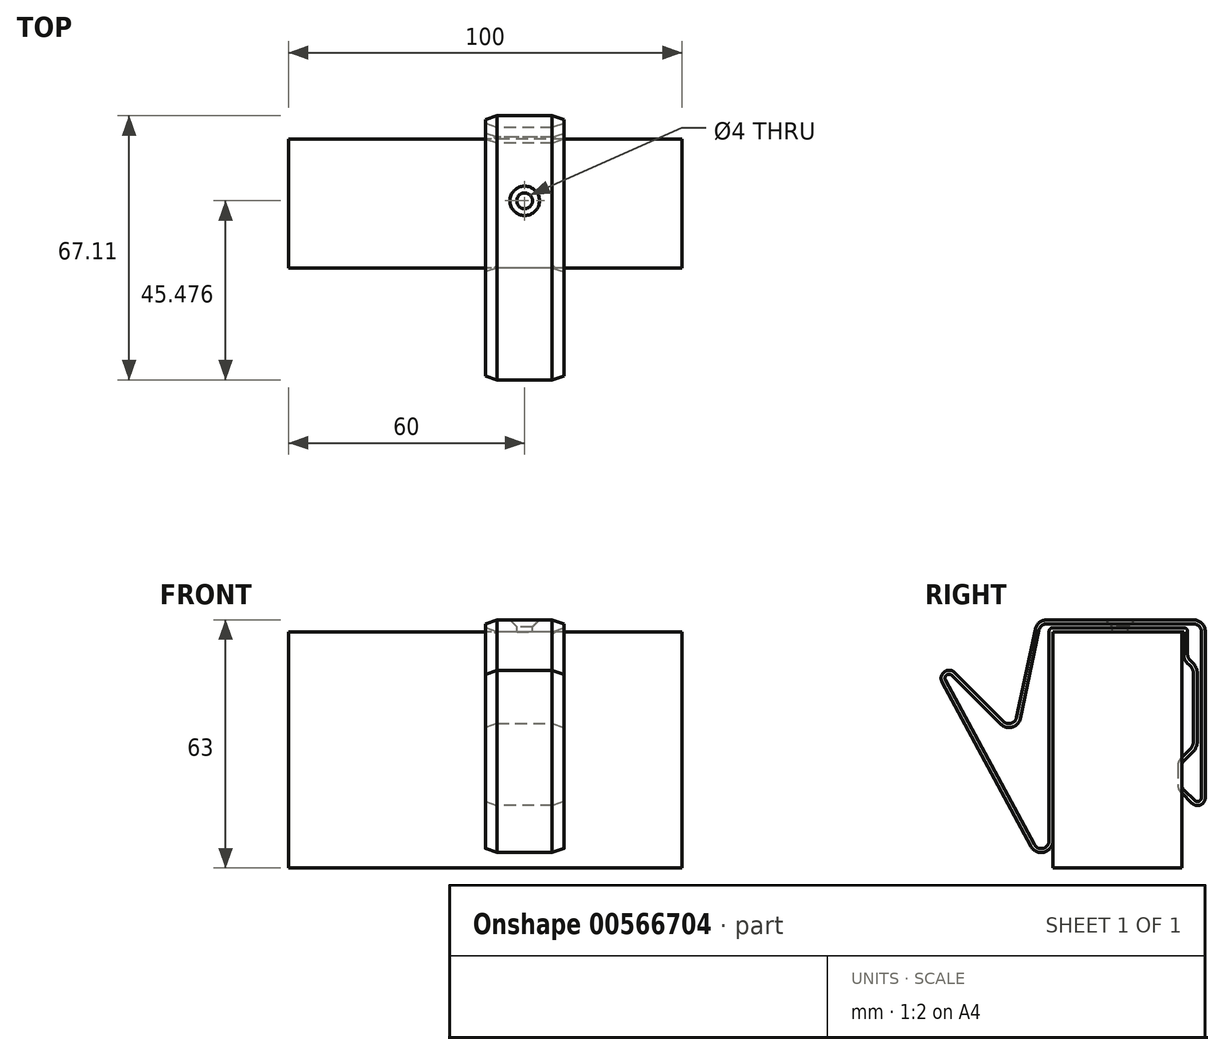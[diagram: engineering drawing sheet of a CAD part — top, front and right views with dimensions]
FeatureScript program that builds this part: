
annotation { "Feature Type Name" : "Feature", "Feature Type Description" : "" }
export const myFeature = defineFeature(function(context is Context, id is Id, definition is map)
    precondition{}
    {
        {
            var Q0;
            Q0=qCreatedBy(makeId("Right.planeOp"),FACE);
            var sketch = newSketch(context, id + "F0", { "sketchPlane" : qUnion([Q0])});
            skLineSegment(sketch, "E0.bottom", {"start": v(0, 0) * mm, "end": v(32.7, 0) * mm});
            skLineSegment(sketch, "E0.top", {"start": v(0, -60) * mm, "end": v(32.7, -60) * mm});
            skLineSegment(sketch, "E0.left", {"start": v(0, 0) * mm, "end": v(0, -60) * mm});
            skLineSegment(sketch, "E0.right", {"start": v(32.7, 0) * mm, "end": v(32.7, -60) * mm});
            skSolve(sketch);
        }
        {
            var Q0;
            Q0=qSketchRegion(id+"F0",true);
            extrude(context, id + "F1", {"entities" : qUnion([Q0]), "depth" : 50 * mm, "hasSecondDirection" : true, "secondDirectionOppositeDirection" : true, "secondDirectionDepth" : 50 * mm});
        }
        {
            var Q0;
            Q0=qCreatedBy(makeId("Right.planeOp"),FACE);
            var sketch = newSketch(context, id + "F2", { "sketchPlane" : qUnion([Q0])});
            skLineSegment(sketch, "E1", {"start": v(0, -65) * mm, "end": v(-28.17, -12.75) * mm});
            skLineSegment(sketch, "E2", {"start": v(-25, -10.38) * mm, "end": v(-10, -25.38) * mm});
            skLineSegment(sketch, "E3", {"start": v(-10, -25.38) * mm, "end": v(-4, 3) * mm});
            skLineSegment(sketch, "E4", {"start": v(-4, 3) * mm, "end": v(38.7, 3) * mm});
            skLineSegment(sketch, "E5", {"start": v(38.7, 3) * mm, "end": v(38.7, -47) * mm});
            skLineSegment(sketch, "E6", {"start": v(38.7, -47) * mm, "end": v(31.7, -40) * mm});
            skLineSegment(sketch, "E7", {"start": v(31.7, -40) * mm, "end": v(31.7, -33) * mm});
            skLineSegment(sketch, "E8", {"start": v(31.7, -33) * mm, "end": v(35.7, -29) * mm});
            skLineSegment(sketch, "E9", {"start": v(35.7, -29) * mm, "end": v(35.7, -9.5) * mm});
            skLineSegment(sketch, "E10", {"start": v(35.7, -9.5) * mm, "end": v(33.2, -7) * mm});
            skLineSegment(sketch, "E11", {"start": v(33.2, -7) * mm, "end": v(33.2, 0) * mm});
            skLineSegment(sketch, "E12", {"start": v(33.2, 0) * mm, "end": v(0, 0) * mm});
            skLineSegment(sketch, "E13", {"start": v(0, 0) * mm, "end": v(0, -65) * mm});
            skArc(sketch, "E14", {"start": v(-25, -10.38) * mm, "mid": v(-27.6, -10.2) * mm, "end": v(-28.17, -12.75) * mm});
            skSolve(sketch);
        }
        {
            var Q0;
            Q0=qSketchRegion(id+"F2",true);
            extrude(context, id + "F3", {"entities" : qUnion([Q0]), "depth" : 20 * mm});
        }
        {
            var Q0;
            Q0=makeQuery(id+"F3.opExtrude","SWEPT_EDGE",EDGE,{"disambiguationData":[OSD([sQuery(id+"F2.wireOp",EDGE,"E1"),sQuery(id+"F2.wireOp",EDGE,"E13")])]});
            fillet(context, id + "F4", {"entities" : qUnion([Q0]), "radius" : 3 * mm, "tangentPropagation" : true, "allowEdgeOverflow" : false});
        }
        {
            var Q0;
            Q0=makeQuery(id+"F3.opExtrude","SWEPT_EDGE",EDGE,{"disambiguationData":[OSD([sQuery(id+"F2.wireOp",EDGE,"E2"),sQuery(id+"F2.wireOp",EDGE,"E3")])]});
            fillet(context, id + "F5", {"entities" : qUnion([Q0]), "radius" : 2 * mm, "tangentPropagation" : true, "allowEdgeOverflow" : false});
        }
        {
            var Q0;
            Q0=makeQuery(id+"F3.opExtrude","SWEPT_EDGE",EDGE,{"disambiguationData":[OSD([sQuery(id+"F2.wireOp",EDGE,"E3"),sQuery(id+"F2.wireOp",EDGE,"E4")])]});
            var Q1;
            Q1=makeQuery(id+"F3.opExtrude","SWEPT_EDGE",EDGE,{"disambiguationData":[OSD([sQuery(id+"F2.wireOp",EDGE,"E4"),sQuery(id+"F2.wireOp",EDGE,"E5")])]});
            fillet(context, id + "F6", {"entities" : qUnion([Q0, Q1]), "radius" : 3 * mm, "tangentPropagation" : true, "allowEdgeOverflow" : false});
        }
        {
            var Q0;
            Q0=makeQuery(id+"F3.opExtrude","SWEPT_EDGE",EDGE,{"disambiguationData":[OSD([sQuery(id+"F2.wireOp",EDGE,"E5"),sQuery(id+"F2.wireOp",EDGE,"E6")])]});
            fillet(context, id + "F7", {"entities" : qUnion([Q0]), "radius" : 2 * mm, "tangentPropagation" : true, "allowEdgeOverflow" : false});
        }
        {
            var Q0;
            Q0=makeQuery(id+"F3.opExtrude","SWEPT_EDGE",EDGE,{"disambiguationData":[OSD([sQuery(id+"F2.wireOp",EDGE,"E10"),sQuery(id+"F2.wireOp",EDGE,"E11")])]});
            var Q1;
            Q1=makeQuery(id+"F3.opExtrude","SWEPT_EDGE",EDGE,{"disambiguationData":[OSD([sQuery(id+"F2.wireOp",EDGE,"E9"),sQuery(id+"F2.wireOp",EDGE,"E10")])]});
            var Q2;
            Q2=makeQuery(id+"F3.opExtrude","SWEPT_EDGE",EDGE,{"disambiguationData":[OSD([sQuery(id+"F2.wireOp",EDGE,"E8"),sQuery(id+"F2.wireOp",EDGE,"E9")])]});
            var Q3;
            Q3=makeQuery(id+"F3.opExtrude","SWEPT_EDGE",EDGE,{"disambiguationData":[OSD([sQuery(id+"F2.wireOp",EDGE,"E7"),sQuery(id+"F2.wireOp",EDGE,"E8")])]});
            var Q4;
            Q4=makeQuery(id+"F3.opExtrude","SWEPT_EDGE",EDGE,{"disambiguationData":[OSD([sQuery(id+"F2.wireOp",EDGE,"E6"),sQuery(id+"F2.wireOp",EDGE,"E7")])]});
            fillet(context, id + "F8", {"entities" : qUnion([Q0, Q1, Q2, Q3, Q4]), "radius" : 3 * mm, "tangentPropagation" : true, "allowEdgeOverflow" : false});
        }
        {
            var Q0;
            Q0=makeQuery(id+"F3.opExtrude","CAP_FACE",FACE,{"disambiguationData":[OSD([sQuery(id+"F2.wireOp",EDGE,"E1"),sQuery(id+"F2.wireOp",EDGE,"E2"),sQuery(id+"F2.wireOp",EDGE,"E3"),sQuery(id+"F2.wireOp",EDGE,"E4"),sQuery(id+"F2.wireOp",EDGE,"E5"),sQuery(id+"F2.wireOp",EDGE,"E6"),sQuery(id+"F2.wireOp",EDGE,"E7"),sQuery(id+"F2.wireOp",EDGE,"E8"),sQuery(id+"F2.wireOp",EDGE,"E9"),sQuery(id+"F2.wireOp",EDGE,"E10"),sQuery(id+"F2.wireOp",EDGE,"E11"),sQuery(id+"F2.wireOp",EDGE,"E12"),sQuery(id+"F2.wireOp",EDGE,"E13"),sQuery(id+"F2.wireOp",EDGE,"E14")])],"isStart":false});
            chamfer(context, id + "F9", {"entities" : qUnion([Q0]), "chamferType" : ChamferType.TWO_OFFSETS, "width1" : 3 * mm, "oppositeDirection" : false, "width2" : 1 * mm, "tangentPropagation" : true});
        }
        {
            var Q0;
            Q0=makeQuery(id+"F3.opExtrude","CAP_FACE",FACE,{"disambiguationData":[OSD([sQuery(id+"F2.wireOp",EDGE,"E1"),sQuery(id+"F2.wireOp",EDGE,"E2"),sQuery(id+"F2.wireOp",EDGE,"E3"),sQuery(id+"F2.wireOp",EDGE,"E4"),sQuery(id+"F2.wireOp",EDGE,"E5"),sQuery(id+"F2.wireOp",EDGE,"E6"),sQuery(id+"F2.wireOp",EDGE,"E7"),sQuery(id+"F2.wireOp",EDGE,"E8"),sQuery(id+"F2.wireOp",EDGE,"E9"),sQuery(id+"F2.wireOp",EDGE,"E10"),sQuery(id+"F2.wireOp",EDGE,"E11"),sQuery(id+"F2.wireOp",EDGE,"E12"),sQuery(id+"F2.wireOp",EDGE,"E13"),sQuery(id+"F2.wireOp",EDGE,"E14")])],"isStart":true});
            chamfer(context, id + "F10", {"entities" : qUnion([Q0]), "chamferType" : ChamferType.TWO_OFFSETS, "width1" : 1 * mm, "oppositeDirection" : false, "width2" : 3 * mm, "tangentPropagation" : true});
        }
        {
            var Q0;
            Q0=makeQuery(id+"F3.opExtrude","SWEPT_FACE",FACE,{"disambiguationData":[OSD([sQuery(id+"F2.wireOp",EDGE,"E4")])]});
            var sketch = newSketch(context, id + "F11", { "sketchPlane" : qUnion([Q0])});
            skLineSegment(sketch, "E15", {"start": v(3, 35.7) * mm, "end": v(17, -1.57) * mm, "construction": true});
            skLineSegment(sketch, "E16", {"start": v(17, 35.7) * mm, "end": v(3, -1.57) * mm, "construction": true});
            skPoint(sketch, "E17", {"position": v(10, 17.07) * mm});
            skSolve(sketch);
        }
        {
            var Q0;
            Q0=sQuery(id+"F11.wireOp",VERTEX,"E17");
            var Q1;
            Q1=makeQuery(id+"F3.opExtrude","SWEPT_BODY",BODY,{"disambiguationData":[OSD([sQuery(id+"F2.wireOp",EDGE,"E1"),sQuery(id+"F2.wireOp",EDGE,"E2"),sQuery(id+"F2.wireOp",EDGE,"E3"),sQuery(id+"F2.wireOp",EDGE,"E4"),sQuery(id+"F2.wireOp",EDGE,"E5"),sQuery(id+"F2.wireOp",EDGE,"E6"),sQuery(id+"F2.wireOp",EDGE,"E7"),sQuery(id+"F2.wireOp",EDGE,"E8"),sQuery(id+"F2.wireOp",EDGE,"E9"),sQuery(id+"F2.wireOp",EDGE,"E10"),sQuery(id+"F2.wireOp",EDGE,"E11"),sQuery(id+"F2.wireOp",EDGE,"E12"),sQuery(id+"F2.wireOp",EDGE,"E13"),sQuery(id+"F2.wireOp",EDGE,"E14")])]});
            hole(context, id + "F12", {"style" : HoleStyle.C_SINK, "holeDiameter" : 4 * mm, "cSinkDiameter" : 7.5 * mm, "endStyle" : HoleEndStyle.THROUGH, "locations" : qUnion([Q0]), "scope" : qUnion([Q1]), "cSinkAngle" : 90 * degree});
        }
        {
            var Q0;
            Q0=makeQuery(id+"F9.opChamfer","BLEND_EDGE",EDGE,{"blendedFrom":[makeQuery(id+"F3.opExtrude","CAP_EDGE",EDGE,{"disambiguationData":[OSD([sQuery(id+"F2.wireOp",EDGE,"E12")])],"isStart":false}),makeQuery(id+"F3.opExtrude","CAP_EDGE",EDGE,{"disambiguationData":[OSD([sQuery(id+"F2.wireOp",EDGE,"E13")])],"isStart":false})],"blendedInto":[]});
            var Q1;
            Q1=makeQuery(id+"F9.opChamfer","BLEND_EDGE",EDGE,{"blendedFrom":[makeQuery(id+"F3.opExtrude","CAP_EDGE",EDGE,{"disambiguationData":[OSD([sQuery(id+"F2.wireOp",EDGE,"E12")])],"isStart":false}),makeQuery(id+"F3.opExtrude","CAP_EDGE",EDGE,{"disambiguationData":[OSD([sQuery(id+"F2.wireOp",EDGE,"E11")])],"isStart":false})],"blendedInto":[]});
            var Q2;
            Q2=makeQuery(id+"F10.opChamfer","BLEND_EDGE",EDGE,{"blendedFrom":[makeQuery(id+"F3.opExtrude","CAP_EDGE",EDGE,{"disambiguationData":[OSD([sQuery(id+"F2.wireOp",EDGE,"E12")])],"isStart":true}),makeQuery(id+"F3.opExtrude","CAP_EDGE",EDGE,{"disambiguationData":[OSD([sQuery(id+"F2.wireOp",EDGE,"E13")])],"isStart":true})],"blendedInto":[]});
            var Q3;
            Q3=makeQuery(id+"F10.opChamfer","BLEND_EDGE",EDGE,{"blendedFrom":[makeQuery(id+"F3.opExtrude","CAP_EDGE",EDGE,{"disambiguationData":[OSD([sQuery(id+"F2.wireOp",EDGE,"E12")])],"isStart":true}),makeQuery(id+"F3.opExtrude","CAP_EDGE",EDGE,{"disambiguationData":[OSD([sQuery(id+"F2.wireOp",EDGE,"E11")])],"isStart":true})],"blendedInto":[]});
            fillet(context, id + "F13", {"entities" : qUnion([Q0, Q1, Q2, Q3]), "radius" : 1 * mm, "tangentPropagation" : true, "allowEdgeOverflow" : false});
        }
    });
